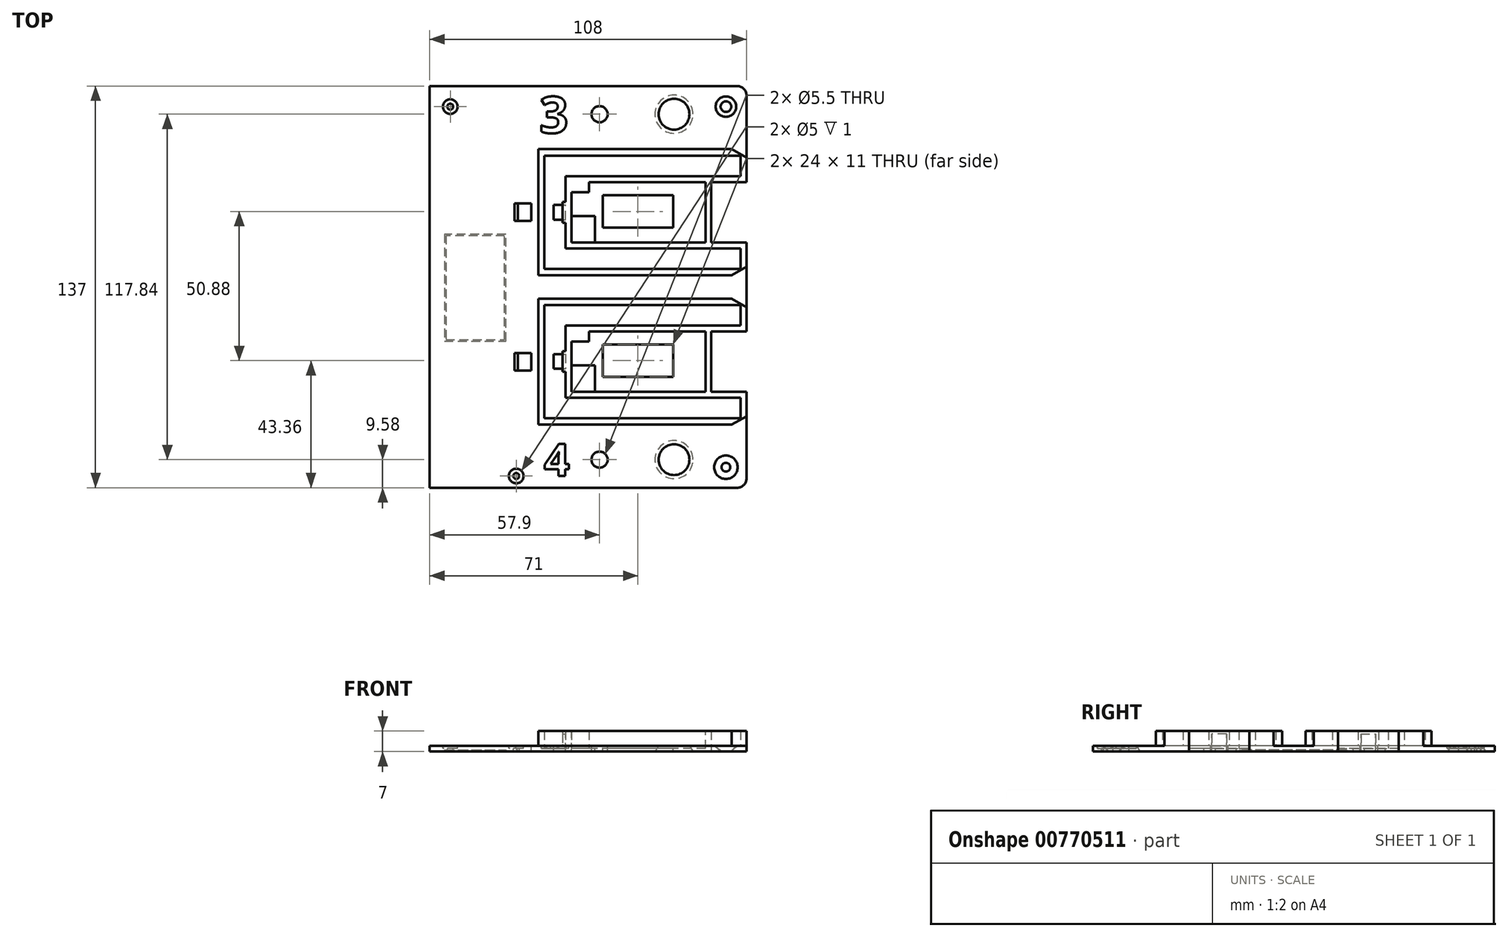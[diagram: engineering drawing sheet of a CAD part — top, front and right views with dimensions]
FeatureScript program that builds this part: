
annotation { "Feature Type Name" : "Feature", "Feature Type Description" : "" }
export const myFeature = defineFeature(function(context is Context, id is Id, definition is map)
    precondition{}
    {
        {
            var Q0;
            Q0=qCreatedBy(makeId("Top.planeOp"),FACE);
            var sketch = newSketch(context, id + "F0", { "sketchPlane" : qUnion([Q0])});
            skLineSegment(sketch, "E0.bottom", {"start": v(-108, 0) * mm, "end": v(0, 0) * mm});
            skLineSegment(sketch, "E1.right", {"start": v(-12, 4.5) * mm, "end": v(-12, 132.5) * mm, "construction": true});
            skLineSegment(sketch, "E2.top", {"start": v(-108, 21.5) * mm, "end": v(-107, 21.5) * mm});
            skLineSegment(sketch, "E2.right", {"start": v(-2, 115.5) * mm, "end": v(-2, 21.5) * mm});
            skLineSegment(sketch, "E3", {"start": v(-225.45, 68.5) * mm, "end": v(18.34, 68.5) * mm, "construction": true});
            skLineSegment(sketch, "E4", {"start": v(-12, 132.5) * mm, "end": v(-210.34, 132.5) * mm, "construction": true});
            skLineSegment(sketch, "E5", {"start": v(-12, 4.5) * mm, "end": v(-202, 4.5) * mm, "construction": true});
            skLineSegment(sketch, "E6", {"start": v(-2, 72.5) * mm, "end": v(-70.94, 72.5) * mm});
            skLineSegment(sketch, "E7", {"start": v(-70.94, 72.5) * mm, "end": v(-70.94, 115.5) * mm, "construction": true});
            skLineSegment(sketch, "E8", {"start": v(-70.94, 115.5) * mm, "end": v(-2, 115.5) * mm, "construction": true});
            skLineSegment(sketch, "E9.bottom", {"start": v(-59.7, 83.64) * mm, "end": v(-14, 83.64) * mm});
            skLineSegment(sketch, "E9.top", {"start": v(-53.7, 104.24) * mm, "end": v(-22.8, 104.24) * mm});
            skLineSegment(sketch, "E9.left", {"start": v(-59.7, 83.64) * mm, "end": v(-59.7, 100.74) * mm});
            skLineSegment(sketch, "E9.right", {"start": v(-14, 83.64) * mm, "end": v(-14, 102.84) * mm});
            skLineSegment(sketch, "E10", {"start": v(-12, 113.24) * mm, "end": v(-12, 74.64) * mm});
            skLineSegment(sketch, "E11", {"start": v(-12, 74.64) * mm, "end": v(-68.94, 74.64) * mm});
            skLineSegment(sketch, "E12", {"start": v(-68.94, 74.64) * mm, "end": v(-68.94, 113.24) * mm, "construction": true});
            skLineSegment(sketch, "E13", {"start": v(-68.94, 113.24) * mm, "end": v(-12, 113.24) * mm, "construction": true});
            skLineSegment(sketch, "E14.bottom", {"start": v(-49, 99.74) * mm, "end": v(-25, 99.74) * mm});
            skLineSegment(sketch, "E14.top", {"start": v(-49, 88.74) * mm, "end": v(-25, 88.74) * mm});
            skLineSegment(sketch, "E14.left", {"start": v(-49, 99.74) * mm, "end": v(-49, 88.74) * mm});
            skLineSegment(sketch, "E14.right", {"start": v(-25, 99.74) * mm, "end": v(-25, 88.74) * mm});
            skLineSegment(sketch, "E15", {"start": v(-25, 94.24) * mm, "end": v(-49, 94.24) * mm, "construction": true});
            skLineSegment(sketch, "E16.bottom", {"start": v(-61.7, 106.24) * mm, "end": v(-12, 106.24) * mm, "construction": true});
            skLineSegment(sketch, "E16.top", {"start": v(-61.7, 81.64) * mm, "end": v(-12, 81.64) * mm});
            skLineSegment(sketch, "E16.left", {"start": v(-61.7, 106.24) * mm, "end": v(-61.7, 81.64) * mm});
            skLineSegment(sketch, "E16.right", {"start": v(-12, 104.24) * mm, "end": v(-12, 83.64) * mm});
            skLineSegment(sketch, "E17", {"start": v(-12, 113.24) * mm, "end": v(-2, 113.24) * mm, "construction": true});
            skLineSegment(sketch, "E18", {"start": v(-12, 74.64) * mm, "end": v(-2, 74.64) * mm});
            skLineSegment(sketch, "E19", {"start": v(-12, 106.24) * mm, "end": v(-2, 106.24) * mm, "construction": true});
            skLineSegment(sketch, "E20", {"start": v(-14, 104.24) * mm, "end": v(-2, 104.24) * mm});
            skLineSegment(sketch, "E21", {"start": v(-14, 83.64) * mm, "end": v(-2, 83.64) * mm});
            skLineSegment(sketch, "E22", {"start": v(-12, 81.64) * mm, "end": v(-2, 81.64) * mm});
            skLineSegment(sketch, "E23.MirrorCS", {"start": v(-12, 23.76) * mm, "end": v(-12, 62.36) * mm});
            skLineSegment(sketch, "E24.MirrorCS", {"start": v(-59.7, 49.86) * mm, "end": v(-59.7, 32.76) * mm});
            skLineSegment(sketch, "E25.MirrorCS", {"start": v(-12, 62.36) * mm, "end": v(-2, 62.36) * mm});
            skLineSegment(sketch, "E26.MirrorCS", {"start": v(-70.94, 21.5) * mm, "end": v(-2, 21.5) * mm});
            skLineSegment(sketch, "E27.MirrorCS", {"start": v(-68.94, 62.36) * mm, "end": v(-68.94, 23.76) * mm});
            skLineSegment(sketch, "E28.MirrorCS", {"start": v(-12, 55.36) * mm, "end": v(-2, 55.36) * mm});
            skLineSegment(sketch, "E29.MirrorCS", {"start": v(-61.7, 30.76) * mm, "end": v(-61.7, 55.36) * mm});
            skLineSegment(sketch, "E30.MirrorCS", {"start": v(-59.7, 32.76) * mm, "end": v(-14, 32.76) * mm});
            skLineSegment(sketch, "E31.MirrorCS", {"start": v(-12, 23.76) * mm, "end": v(-2, 23.76) * mm});
            skLineSegment(sketch, "E32.MirrorCS", {"start": v(-12, 62.36) * mm, "end": v(-68.94, 62.36) * mm});
            skLineSegment(sketch, "E33.MirrorCS", {"start": v(-61.7, 55.36) * mm, "end": v(-12, 55.36) * mm});
            skLineSegment(sketch, "E34.MirrorCS", {"start": v(-14, 53.36) * mm, "end": v(-2, 53.36) * mm});
            skLineSegment(sketch, "E35.MirrorCS", {"start": v(-2, 64.5) * mm, "end": v(-70.94, 64.5) * mm});
            skLineSegment(sketch, "E36.MirrorCS", {"start": v(-61.7, 30.76) * mm, "end": v(-12, 30.76) * mm});
            skLineSegment(sketch, "E37.MirrorCS", {"start": v(-14, 32.76) * mm, "end": v(-2, 32.76) * mm});
            skLineSegment(sketch, "E38.MirrorCS", {"start": v(-68.94, 23.76) * mm, "end": v(-12, 23.76) * mm});
            skLineSegment(sketch, "E39.MirrorCS", {"start": v(-53.7, 53.36) * mm, "end": v(-14, 53.36) * mm});
            skLineSegment(sketch, "E40.MirrorCS", {"start": v(-12, 32.76) * mm, "end": v(-12, 53.36) * mm});
            skLineSegment(sketch, "E41.MirrorCS", {"start": v(-14, 53.36) * mm, "end": v(-14, 32.76) * mm});
            skLineSegment(sketch, "E42.MirrorCS", {"start": v(-12, 30.76) * mm, "end": v(-2, 30.76) * mm});
            skLineSegment(sketch, "E43", {"start": v(-107, 148.51) * mm, "end": v(-107, -58.81) * mm, "construction": true});
            skCircle(sketch, "E44.MirrorC", {"center": v(-50.1, 127.42) * mm, "radius": 2.75 * mm});
            skCircle(sketch, "E45.MirrorC", {"center": v(-24.7, 127.42) * mm, "radius": 5.25 * mm, "construction": true});
            skCircle(sketch, "E46.MirrorC", {"center": v(-50.1, 9.58) * mm, "radius": 2.75 * mm});
            skCircle(sketch, "E47.MirrorC", {"center": v(-24.7, 9.58) * mm, "radius": 5.25 * mm, "construction": true});
            skLineSegment(sketch, "E48.bottom", {"start": v(-49, 37.86) * mm, "end": v(-25, 37.86) * mm});
            skLineSegment(sketch, "E48.top", {"start": v(-49, 48.86) * mm, "end": v(-25, 48.86) * mm});
            skLineSegment(sketch, "E48.left", {"start": v(-49, 37.86) * mm, "end": v(-49, 48.86) * mm});
            skLineSegment(sketch, "E48.right", {"start": v(-25, 37.86) * mm, "end": v(-25, 48.86) * mm});
            skLineSegment(sketch, "E49", {"start": v(-49, 43.36) * mm, "end": v(-25, 43.36) * mm, "construction": true});
            skLineSegment(sketch, "E50", {"start": v(-2, 115.5) * mm, "end": v(0, 115.5) * mm});
            skLineSegment(sketch, "E51", {"start": v(-2, 72.5) * mm, "end": v(0, 72.5) * mm});
            skLineSegment(sketch, "E52", {"start": v(0, 137) * mm, "end": v(0, 0) * mm});
            skLineSegment(sketch, "E53", {"start": v(-59.7, 92.64) * mm, "end": v(-51.7, 92.64) * mm});
            skLineSegment(sketch, "E54", {"start": v(-51.7, 92.64) * mm, "end": v(-51.7, 83.64) * mm});
            skLineSegment(sketch, "E55", {"start": v(-59.7, 41.76) * mm, "end": v(-51.7, 41.76) * mm});
            skLineSegment(sketch, "E56", {"start": v(-51.7, 41.76) * mm, "end": v(-51.7, 32.76) * mm});
            skLineSegment(sketch, "E57", {"start": v(-53.7, 104.24) * mm, "end": v(-53.7, 100.74) * mm});
            skLineSegment(sketch, "E58", {"start": v(-53.7, 100.74) * mm, "end": v(-59.7, 100.74) * mm});
            skPoint(sketch, "E59.orphan", {"position": v(-59.7, 104.24) * mm});
            skLineSegment(sketch, "E60", {"start": v(-53.7, 53.36) * mm, "end": v(-53.7, 49.86) * mm});
            skLineSegment(sketch, "E61", {"start": v(-53.7, 49.86) * mm, "end": v(-59.7, 49.86) * mm});
            skPoint(sketch, "E62.orphan", {"position": v(-59.7, 53.36) * mm});
            skText(sketch, "E63", { "text": "3", "fontName": "OpenSans-Bold.ttf"});
            skText(sketch, "E64", { "text": "4", "fontName": "OpenSans-Bold.ttf"});
            skLineSegment(sketch, "E65", {"start": v(-182.8, 118.88) * mm, "end": v(-182.8, 145.8) * mm, "construction": true});
            skLineSegment(sketch, "E66", {"start": v(-166.65, 144.92) * mm, "end": v(-166.65, 118.26) * mm, "construction": true});
            skLineSegment(sketch, "E67", {"start": v(-108, 72.5) * mm, "end": v(-107, 72.5) * mm});
            skLineSegment(sketch, "E68", {"start": v(-108, 137) * mm, "end": v(-108, 0) * mm});
            skLineSegment(sketch, "E69.trimOffspring", {"start": v(-108, 137) * mm, "end": v(0, 137) * mm});
            skLineSegment(sketch, "E70", {"start": v(-70.94, 64.5) * mm, "end": v(-70.94, 21.5) * mm});
            skLineSegment(sketch, "E71.trimOffspring", {"start": v(-70.94, 72.5) * mm, "end": v(-64, 72.5) * mm});
            skLineSegment(sketch, "E72", {"start": v(-22.8, 104.24) * mm, "end": v(-14, 104.24) * mm});
            skLineSegment(sketch, "E73", {"start": v(-14, 104.24) * mm, "end": v(-14, 102.84) * mm});
            const initialGuessF0  = {"E63": [-0.06894, 0.004, 1, 0, 0.011], "E64": [-0.07094, 0.121, 1, 0, 0.012]};
            skSetInitialGuess(sketch, initialGuessF0);
            skSolve(sketch);
        }
        {
            var Q0;
            Q0=qCreatedBy(makeId("Top.planeOp"),FACE);
            var sketch = newSketch(context, id + "F1", { "sketchPlane" : qUnion([Q0])});
            skLineSegment(sketch, "E74.bottom", {"start": v(-108, 0) * mm, "end": v(0, 0) * mm});
            skLineSegment(sketch, "E74.top", {"start": v(-108, 137) * mm, "end": v(0, 137) * mm});
            skLineSegment(sketch, "E74.left", {"start": v(-108, 0) * mm, "end": v(-108, 137) * mm});
            skLineSegment(sketch, "E74.right", {"start": v(0, 0) * mm, "end": v(0, 137) * mm});
            skSolve(sketch);
        }
        {
            var Q0;
            Q0=qSketchRegion(id+"F1",true);
            extrude(context, id + "F2", {"entities" : qUnion([Q0]), "depth" : 2 * mm, "offsetDistance" : 25 * mm});
        }
        {
            var Q0;
            Q0=makeQuery(id+"F2.opExtrude","CAP_FACE",FACE,{"disambiguationData":[OSD([sQuery(id+"F1.wireOp",EDGE,"E74.bottom"),sQuery(id+"F1.wireOp",EDGE,"E74.top"),sQuery(id+"F1.wireOp",EDGE,"E74.left"),sQuery(id+"F1.wireOp",EDGE,"E74.right")])],"isStart":false});
            var sketch = newSketch(context, id + "F3", { "sketchPlane" : qUnion([Q0])});
            skLineSegment(sketch, "E75.bottom", {"start": v(-70.94, 115.5) * mm, "end": v(0, 115.5) * mm});
            skLineSegment(sketch, "E75.top", {"start": v(-70.94, 72.5) * mm, "end": v(0, 72.5) * mm});
            skLineSegment(sketch, "E75.left", {"start": v(-70.94, 115.5) * mm, "end": v(-70.94, 72.5) * mm});
            skLineSegment(sketch, "E75.right", {"start": v(0, 115.5) * mm, "end": v(0, 72.5) * mm});
            skLineSegment(sketch, "E76.bottom", {"start": v(-68.94, 62.36) * mm, "end": v(-2, 62.36) * mm});
            skLineSegment(sketch, "E76.top", {"start": v(-68.94, 23.76) * mm, "end": v(-2, 23.76) * mm});
            skLineSegment(sketch, "E76.left", {"start": v(-68.94, 62.36) * mm, "end": v(-68.94, 23.76) * mm});
            skLineSegment(sketch, "E76.right", {"start": v(0, 62.36) * mm, "end": v(0, 23.76) * mm});
            skLineSegment(sketch, "E77.bottom", {"start": v(-70.94, 64.5) * mm, "end": v(0, 64.5) * mm});
            skLineSegment(sketch, "E77.top", {"start": v(-70.94, 21.5) * mm, "end": v(0, 21.5) * mm});
            skLineSegment(sketch, "E77.left", {"start": v(-70.94, 64.5) * mm, "end": v(-70.94, 21.5) * mm});
            skLineSegment(sketch, "E77.right", {"start": v(0, 64.5) * mm, "end": v(0, 21.5) * mm});
            skLineSegment(sketch, "E78.bottom", {"start": v(-68.94, 113.24) * mm, "end": v(-2, 113.24) * mm});
            skLineSegment(sketch, "E78.top", {"start": v(-68.94, 74.64) * mm, "end": v(-2, 74.64) * mm});
            skLineSegment(sketch, "E78.left", {"start": v(-68.94, 113.24) * mm, "end": v(-68.94, 74.64) * mm});
            skLineSegment(sketch, "E78.right", {"start": v(-2, 113.24) * mm, "end": v(-2, 74.64) * mm});
            skLineSegment(sketch, "E79", {"start": v(-2, 62.36) * mm, "end": v(-2, 23.76) * mm});
            skLineSegment(sketch, "E80.bottom", {"start": v(-12, 104.24) * mm, "end": v(-2, 104.24) * mm});
            skLineSegment(sketch, "E80.top", {"start": v(-12, 83.64) * mm, "end": v(-2, 83.64) * mm});
            skLineSegment(sketch, "E80.left", {"start": v(-12, 104.24) * mm, "end": v(-12, 83.64) * mm});
            skLineSegment(sketch, "E80.right", {"start": v(-2, 104.24) * mm, "end": v(-2, 83.64) * mm});
            skLineSegment(sketch, "E81.bottom", {"start": v(-12, 53.36) * mm, "end": v(-2, 53.36) * mm});
            skLineSegment(sketch, "E81.top", {"start": v(-12, 32.76) * mm, "end": v(-2, 32.76) * mm});
            skLineSegment(sketch, "E81.left", {"start": v(-12, 53.36) * mm, "end": v(-12, 32.76) * mm});
            skLineSegment(sketch, "E81.right", {"start": v(-2, 53.36) * mm, "end": v(-2, 32.76) * mm});
            skLineSegment(sketch, "E82.bottom", {"start": v(-61.7, 55.36) * mm, "end": v(-2, 55.36) * mm});
            skLineSegment(sketch, "E82.top", {"start": v(-61.7, 30.76) * mm, "end": v(-2, 30.76) * mm});
            skLineSegment(sketch, "E82.left", {"start": v(-61.7, 55.36) * mm, "end": v(-61.7, 30.76) * mm});
            skLineSegment(sketch, "E83.bottom", {"start": v(-61.7, 106.24) * mm, "end": v(-2, 106.24) * mm});
            skLineSegment(sketch, "E83.top", {"start": v(-61.7, 81.64) * mm, "end": v(-2, 81.64) * mm});
            skLineSegment(sketch, "E83.left", {"start": v(-61.7, 106.24) * mm, "end": v(-61.7, 81.64) * mm});
            skLineSegment(sketch, "E84", {"start": v(-14, 102.84) * mm, "end": v(-14, 83.64) * mm});
            skLineSegment(sketch, "E85", {"start": v(-14, 102.84) * mm, "end": v(-22.8, 102.84) * mm});
            skLineSegment(sketch, "E86", {"start": v(-22.8, 102.84) * mm, "end": v(-22.8, 104.24) * mm});
            skLineSegment(sketch, "E87", {"start": v(-22.8, 104.24) * mm, "end": v(-53.7, 104.24) * mm});
            skLineSegment(sketch, "E88", {"start": v(-53.7, 104.24) * mm, "end": v(-53.7, 100.74) * mm});
            skLineSegment(sketch, "E89", {"start": v(-53.7, 100.74) * mm, "end": v(-59.7, 100.74) * mm});
            skLineSegment(sketch, "E90", {"start": v(-59.7, 100.74) * mm, "end": v(-59.7, 92.64) * mm});
            skLineSegment(sketch, "E91", {"start": v(-59.7, 92.64) * mm, "end": v(-51.7, 92.64) * mm});
            skLineSegment(sketch, "E92", {"start": v(-51.7, 92.64) * mm, "end": v(-51.7, 83.64) * mm});
            skLineSegment(sketch, "E93", {"start": v(-51.7, 83.64) * mm, "end": v(-14, 83.64) * mm});
            skLineSegment(sketch, "E94", {"start": v(-14, 51.96) * mm, "end": v(-22.8, 51.96) * mm});
            skLineSegment(sketch, "E95", {"start": v(-22.8, 51.96) * mm, "end": v(-22.8, 53.36) * mm});
            skLineSegment(sketch, "E96", {"start": v(-22.8, 53.36) * mm, "end": v(-53.7, 53.36) * mm});
            skLineSegment(sketch, "E97", {"start": v(-53.7, 53.36) * mm, "end": v(-53.7, 49.86) * mm});
            skLineSegment(sketch, "E98", {"start": v(-53.7, 49.86) * mm, "end": v(-59.7, 49.86) * mm});
            skLineSegment(sketch, "E99", {"start": v(-59.7, 49.86) * mm, "end": v(-59.7, 41.76) * mm});
            skLineSegment(sketch, "E100", {"start": v(-59.7, 41.76) * mm, "end": v(-51.7, 41.76) * mm});
            skLineSegment(sketch, "E101", {"start": v(-51.7, 41.76) * mm, "end": v(-51.7, 32.76) * mm});
            skLineSegment(sketch, "E102", {"start": v(-51.7, 32.76) * mm, "end": v(-14, 32.76) * mm});
            skLineSegment(sketch, "E103", {"start": v(-14, 32.76) * mm, "end": v(-14, 51.96) * mm});
            skSolve(sketch);
        }
        {
            var Q0;
            Q0=qSketchRegion(id+"F3",true);
            var Q1;
            {var subQ1=sQuery(id+"F3.wireOp",EDGE,"E80.bottom");Q1=makeQuery(id+"F3.imprint","IMPRINT",FACE,{"disambiguationData":[TD([[makeQuery(id+"F3.imprint","IMPRINT",EDGE,{"derivedFrom":subQ1}),1.0]])]});}
            var Q2;
            {var subQ2=sQuery(id+"F3.wireOp",EDGE,"E81.bottom");Q2=makeQuery(id+"F3.imprint","IMPRINT",FACE,{"disambiguationData":[TD([[makeQuery(id+"F3.imprint","IMPRINT",EDGE,{"derivedFrom":subQ2}),1.0]])]});}
            extrude(context, id + "F4", {"entities" : qUnion([Q0, Q1, Q2]), "operationType" : NewBodyOperationType.ADD, "depth" : 5 * mm, "offsetDistance" : 25 * mm});
        }
        {
            var Q0;
            {var subQ0=sQuery(id+"F1.wireOp",EDGE,"E74.bottom");var subQ1=sQuery(id+"F1.wireOp",EDGE,"E74.right");var subQ2=sQuery(id+"F1.wireOp",EDGE,"E74.top");var subQ3=sQuery(id+"F1.wireOp",EDGE,"E74.left");Q0=makeQuery(id+"F4.boolean.opBoolean","SPLIT",FACE,{"disambiguationData":[TD([makeQuery(id+"F2.opExtrude","SWEPT_FACE",FACE,{"disambiguationData":[OSD([subQ0])]})])],"derivedFrom":makeQuery(id+"F2.opExtrude","CAP_FACE",FACE,{"disambiguationData":[OSD([subQ0,subQ2,subQ3,subQ1])],"isStart":false})});}
            var sketch = newSketch(context, id + "F5", { "sketchPlane" : qUnion([Q0])});
            skCircle(sketch, "E104", {"center": v(-24.7, 127.42) * mm, "radius": 5.25 * mm});
            skCircle(sketch, "E105", {"center": v(-50.1, 127.42) * mm, "radius": 2.75 * mm});
            skCircle(sketch, "E106", {"center": v(-24.7, 9.58) * mm, "radius": 5.25 * mm});
            skCircle(sketch, "E107", {"center": v(-50.1, 9.58) * mm, "radius": 2.75 * mm});
            skLineSegment(sketch, "E108.bottom", {"start": v(-12, 83.64) * mm, "end": v(-2, 83.64) * mm});
            skLineSegment(sketch, "E108.top", {"start": v(-12, 104.24) * mm, "end": v(-2, 104.24) * mm});
            skLineSegment(sketch, "E108.left", {"start": v(-12, 83.64) * mm, "end": v(-12, 104.24) * mm});
            skLineSegment(sketch, "E108.right", {"start": v(-2, 83.64) * mm, "end": v(-2, 104.24) * mm});
            skLineSegment(sketch, "E109.bottom", {"start": v(-12, 32.76) * mm, "end": v(-2, 32.76) * mm});
            skLineSegment(sketch, "E109.top", {"start": v(-12, 53.36) * mm, "end": v(-2, 53.36) * mm});
            skLineSegment(sketch, "E109.left", {"start": v(-12, 32.76) * mm, "end": v(-12, 53.36) * mm});
            skLineSegment(sketch, "E109.right", {"start": v(-2, 32.76) * mm, "end": v(-2, 53.36) * mm});
            skLineSegment(sketch, "E110.bottom", {"start": v(-49, 88.74) * mm, "end": v(-25, 88.74) * mm});
            skLineSegment(sketch, "E110.top", {"start": v(-49, 99.74) * mm, "end": v(-25, 99.74) * mm});
            skLineSegment(sketch, "E110.left", {"start": v(-49, 88.74) * mm, "end": v(-49, 99.74) * mm});
            skLineSegment(sketch, "E110.right", {"start": v(-25, 88.74) * mm, "end": v(-25, 99.74) * mm});
            skLineSegment(sketch, "E111.bottom", {"start": v(-49, 37.86) * mm, "end": v(-25, 37.86) * mm});
            skLineSegment(sketch, "E111.top", {"start": v(-49, 48.86) * mm, "end": v(-25, 48.86) * mm});
            skLineSegment(sketch, "E111.left", {"start": v(-49, 37.86) * mm, "end": v(-49, 48.86) * mm});
            skLineSegment(sketch, "E111.right", {"start": v(-25, 37.86) * mm, "end": v(-25, 48.86) * mm});
            skSolve(sketch);
        }
        {
            var Q0;
            Q0=qSketchRegion(id+"F5",true);
            extrude(context, id + "F6", {"entities" : qUnion([Q0]), "operationType" : NewBodyOperationType.REMOVE, "oppositeDirection" : true, "depth" : 2 * mm, "offsetDistance" : 25 * mm});
        }
        {
            var Q0;
            {var subQ0=sQuery(id+"F1.wireOp",EDGE,"E74.bottom");var subQ1=sQuery(id+"F1.wireOp",EDGE,"E74.right");var subQ2=sQuery(id+"F1.wireOp",EDGE,"E74.top");var subQ3=sQuery(id+"F1.wireOp",EDGE,"E74.left");Q0=makeQuery(id+"F4.boolean.opBoolean","SPLIT",FACE,{"disambiguationData":[TD([makeQuery(id+"F2.opExtrude","SWEPT_FACE",FACE,{"disambiguationData":[OSD([subQ0])]})])],"derivedFrom":makeQuery(id+"F2.opExtrude","CAP_FACE",FACE,{"disambiguationData":[OSD([subQ0,subQ2,subQ3,subQ1])],"isStart":false})});}
            var sketch = newSketch(context, id + "F7", { "sketchPlane" : qUnion([Q0])});
            skCircle(sketch, "E112", {"center": v(-7, 130) * mm, "radius": 4 * mm, "construction": true});
            skCircle(sketch, "E113", {"center": v(-101, 130) * mm, "radius": 1 * mm});
            skCircle(sketch, "E114", {"center": v(-7, 7) * mm, "radius": 4 * mm, "construction": true});
            skCircle(sketch, "E115", {"center": v(-78.5, 4) * mm, "radius": 1 * mm});
            skSolve(sketch);
        }
        {
            var Q0;
            Q0=qSketchRegion(id+"F7",true);
            var Q1;
            Q1=qConstructionFilter(qBodyType(qCreatedBy(id+"F7",EDGE),BodyType.WIRE),ConstructionObject.NO);
            extrude(context, id + "F8", {"entities" : qUnion([Q0]), "operationType" : NewBodyOperationType.REMOVE, "surfaceEntities" : qUnion([Q1]), "oppositeDirection" : true, "depth" : 2 * mm, "offsetDistance" : 25 * mm});
        }
        {
            var Q0;
            Q0=makeQuery(id+"F2.opExtrude","SWEPT_EDGE",EDGE,{"disambiguationData":[OSD([sQuery(id+"F1.wireOp",EDGE,"E74.top"),sQuery(id+"F1.wireOp",EDGE,"E74.right")])]});
            var Q1;
            Q1=makeQuery(id+"F2.opExtrude","SWEPT_EDGE",EDGE,{"disambiguationData":[OSD([sQuery(id+"F1.wireOp",EDGE,"E74.bottom"),sQuery(id+"F1.wireOp",EDGE,"E74.right")])]});
            fillet(context, id + "F9", {"entities" : qUnion([Q0, Q1]), "radius" : 3.17 * mm, "tangentPropagation" : true, "allowEdgeOverflow" : false});
        }
        {
            var Q0;
            {var subQ0=sQuery(id+"F1.wireOp",EDGE,"E74.bottom");var subQ1=sQuery(id+"F1.wireOp",EDGE,"E74.right");var subQ2=sQuery(id+"F1.wireOp",EDGE,"E74.top");var subQ3=sQuery(id+"F1.wireOp",EDGE,"E74.left");Q0=makeQuery(id+"F4.boolean.opBoolean","SPLIT",FACE,{"disambiguationData":[TD([makeQuery(id+"F2.opExtrude","SWEPT_FACE",FACE,{"disambiguationData":[OSD([subQ0])]})])],"derivedFrom":makeQuery(id+"F2.opExtrude","CAP_FACE",FACE,{"disambiguationData":[OSD([subQ0,subQ2,subQ3,subQ1])],"isStart":false})});}
            var sketch = newSketch(context, id + "F10", { "sketchPlane" : qUnion([Q0])});
            skText(sketch, "E116", { "text": "3", "fontName": "OpenSans-Bold.ttf"});
            skText(sketch, "E117", { "text": "4", "fontName": "OpenSans-Bold.ttf"});
            const initialGuessF10  = {"E116": [-0.07066, 0.121, 1, 0, 0.01246], "E117": [-0.069, 0.004, 1, 0, 0.011]};
            skSetInitialGuess(sketch, initialGuessF10);
            skSolve(sketch);
        }
        {
            var Q0;
            Q0=qSketchRegion(id+"F10",true);
            extrude(context, id + "F11", {"entities" : qUnion([Q0]), "operationType" : NewBodyOperationType.REMOVE, "oppositeDirection" : true, "depth" : 1 * mm, "offsetDistance" : 25 * mm});
        }
        {
            var Q0;
            Q0=makeQuery(id+"F4.opExtrude","CAP_FACE",FACE,{"disambiguationData":[OSD([sQuery(id+"F3.wireOp",EDGE,"E75.bottom"),sQuery(id+"F3.wireOp",EDGE,"E75.top"),sQuery(id+"F3.wireOp",EDGE,"E75.left"),sQuery(id+"F3.wireOp",EDGE,"E75.right"),sQuery(id+"F3.wireOp",EDGE,"E78.bottom"),sQuery(id+"F3.wireOp",EDGE,"E78.top"),sQuery(id+"F3.wireOp",EDGE,"E78.left"),sQuery(id+"F3.wireOp",EDGE,"E78.right"),sQuery(id+"F3.wireOp",EDGE,"E80.bottom"),sQuery(id+"F3.wireOp",EDGE,"E80.top"),sQuery(id+"F3.wireOp",EDGE,"E80.left"),sQuery(id+"F3.wireOp",EDGE,"E80.right"),sQuery(id+"F3.wireOp",EDGE,"E83.bottom"),sQuery(id+"F3.wireOp",EDGE,"E83.top"),sQuery(id+"F3.wireOp",EDGE,"E83.left"),sQuery(id+"F3.wireOp",EDGE,"E84"),sQuery(id+"F3.wireOp",EDGE,"E85"),sQuery(id+"F3.wireOp",EDGE,"E86"),sQuery(id+"F3.wireOp",EDGE,"E87"),sQuery(id+"F3.wireOp",EDGE,"E88"),sQuery(id+"F3.wireOp",EDGE,"E89"),sQuery(id+"F3.wireOp",EDGE,"E90"),sQuery(id+"F3.wireOp",EDGE,"E91"),sQuery(id+"F3.wireOp",EDGE,"E92"),sQuery(id+"F3.wireOp",EDGE,"E93")])],"isStart":false});
            var sketch = newSketch(context, id + "F12", { "sketchPlane" : qUnion([Q0])});
            skLineSegment(sketch, "E118.bottom", {"start": v(-59.7, 83.64) * mm, "end": v(-51.7, 83.64) * mm});
            skLineSegment(sketch, "E118.top", {"start": v(-59.7, 92.64) * mm, "end": v(-51.7, 92.64) * mm});
            skLineSegment(sketch, "E118.left", {"start": v(-59.7, 83.64) * mm, "end": v(-59.7, 92.64) * mm});
            skLineSegment(sketch, "E118.right", {"start": v(-51.7, 83.64) * mm, "end": v(-51.7, 92.64) * mm});
            skLineSegment(sketch, "E119.bottom", {"start": v(-59.7, 32.76) * mm, "end": v(-51.7, 32.76) * mm});
            skLineSegment(sketch, "E119.top", {"start": v(-59.7, 41.76) * mm, "end": v(-51.7, 41.76) * mm});
            skLineSegment(sketch, "E119.left", {"start": v(-59.7, 32.76) * mm, "end": v(-59.7, 41.76) * mm});
            skLineSegment(sketch, "E119.right", {"start": v(-51.7, 32.76) * mm, "end": v(-51.7, 41.76) * mm});
            skLineSegment(sketch, "E120.bottom", {"start": v(-4.45, 83.64) * mm, "end": v(2.07, 83.64) * mm});
            skLineSegment(sketch, "E120.top", {"start": v(-4.45, 104.24) * mm, "end": v(2.07, 104.24) * mm});
            skLineSegment(sketch, "E120.left", {"start": v(-4.45, 83.64) * mm, "end": v(-4.45, 104.24) * mm});
            skLineSegment(sketch, "E120.right", {"start": v(2.07, 83.64) * mm, "end": v(2.07, 104.24) * mm});
            skLineSegment(sketch, "E121.bottom", {"start": v(-6.26, 53.36) * mm, "end": v(9.3, 53.36) * mm});
            skLineSegment(sketch, "E121.top", {"start": v(-6.26, 32.76) * mm, "end": v(9.3, 32.76) * mm});
            skLineSegment(sketch, "E121.left", {"start": v(-6.26, 53.36) * mm, "end": v(-6.26, 32.76) * mm});
            skLineSegment(sketch, "E121.right", {"start": v(9.3, 53.36) * mm, "end": v(9.3, 32.76) * mm});
            skSolve(sketch);
        }
        {
            var Q0;
            Q0=qSketchRegion(id+"F12",true);
            extrude(context, id + "F13", {"entities" : qUnion([Q0]), "operationType" : NewBodyOperationType.REMOVE, "endBound" : BoundingType.THROUGH_ALL, "oppositeDirection" : true, "depth" : 25 * mm, "offsetDistance" : 25 * mm});
        }
        {
            var Q0;
            Q0=makeQuery(id+"F2.opExtrude","CAP_FACE",FACE,{"disambiguationData":[OSD([sQuery(id+"F1.wireOp",EDGE,"E74.bottom"),sQuery(id+"F1.wireOp",EDGE,"E74.top"),sQuery(id+"F1.wireOp",EDGE,"E74.left"),sQuery(id+"F1.wireOp",EDGE,"E74.right")])],"isStart":true});
            var sketch = newSketch(context, id + "F14", { "sketchPlane" : qUnion([Q0])});
            skCircle(sketch, "E122", {"center": v(-7, -130) * mm, "radius": 1.81 * mm});
            skSolve(sketch);
        }
        {
            var Q0;
            {var subQ6=sQuery(id+"F1.wireOp",EDGE,"E74.right");var subQ8=sQuery(id+"F1.wireOp",EDGE,"E74.top");var subQ11=sQuery(id+"F1.wireOp",EDGE,"E74.left");var subQ14=sQuery(id+"F1.wireOp",EDGE,"E74.bottom");var subQ15=makeQuery(id+"F2.opExtrude","SWEPT_FACE",FACE,{"disambiguationData":[OSD([subQ14])]});Q0=makeQuery(id+"F11.boolean.opBoolean","SPLIT",FACE,{"disambiguationData":[TD([subQ15])],"derivedFrom":makeQuery(id+"F4.boolean.opBoolean","SPLIT",FACE,{"disambiguationData":[TD([subQ15])],"derivedFrom":makeQuery(id+"F2.opExtrude","CAP_FACE",FACE,{"disambiguationData":[OSD([subQ14,subQ8,subQ11,subQ6])],"isStart":false})})});}
            var sketch = newSketch(context, id + "F15", { "sketchPlane" : qUnion([Q0])});
            skCircle(sketch, "E123", {"center": v(-7, 130) * mm, "radius": 3.5 * mm});
            skSolve(sketch);
        }
        {
            var Q1;
            Q1=qSketchRegion(id+"F15",true);
            var Q2;
            Q2=qSketchRegion(id+"F14",true);
            loft(context, id + "F16", {"operationType" : NewBodyOperationType.REMOVE, "sheetProfilesArray" : [{ "sheetProfileEntities" : qUnion([Q1]) }, { "sheetProfileEntities" : qUnion([Q2]) }]});
        }
        {
            var Q0;
            {var subQ6=sQuery(id+"F1.wireOp",EDGE,"E74.right");var subQ8=sQuery(id+"F1.wireOp",EDGE,"E74.top");var subQ11=sQuery(id+"F1.wireOp",EDGE,"E74.left");var subQ14=sQuery(id+"F1.wireOp",EDGE,"E74.bottom");var subQ15=makeQuery(id+"F2.opExtrude","SWEPT_FACE",FACE,{"disambiguationData":[OSD([subQ14])]});Q0=makeQuery(id+"F11.boolean.opBoolean","SPLIT",FACE,{"disambiguationData":[TD([subQ15])],"derivedFrom":makeQuery(id+"F4.boolean.opBoolean","SPLIT",FACE,{"disambiguationData":[TD([subQ15])],"derivedFrom":makeQuery(id+"F2.opExtrude","CAP_FACE",FACE,{"disambiguationData":[OSD([subQ14,subQ8,subQ11,subQ6])],"isStart":false})})});}
            var sketch = newSketch(context, id + "F17", { "sketchPlane" : qUnion([Q0])});
            skCircle(sketch, "E124", {"center": v(-7, 7) * mm, "radius": 4 * mm});
            skSolve(sketch);
        }
        {
            var Q0;
            Q0=makeQuery(id+"F2.opExtrude","CAP_FACE",FACE,{"disambiguationData":[OSD([sQuery(id+"F1.wireOp",EDGE,"E74.bottom"),sQuery(id+"F1.wireOp",EDGE,"E74.top"),sQuery(id+"F1.wireOp",EDGE,"E74.left"),sQuery(id+"F1.wireOp",EDGE,"E74.right")])],"isStart":true});
            var sketch = newSketch(context, id + "F18", { "sketchPlane" : qUnion([Q0])});
            skCircle(sketch, "E125", {"center": v(-7, -7) * mm, "radius": 1.5 * mm});
            skSolve(sketch);
        }
        {
            var Q1;
            Q1=qSketchRegion(id+"F18",true);
            var Q2;
            Q2=qSketchRegion(id+"F17",true);
            loft(context, id + "F19", {"operationType" : NewBodyOperationType.REMOVE, "sheetProfilesArray" : [{ "sheetProfileEntities" : qUnion([Q1]) }, { "sheetProfileEntities" : qUnion([Q2]) }]});
        }
        {
            var Q0;
            {var subQ6=sQuery(id+"F1.wireOp",EDGE,"E74.right");var subQ8=sQuery(id+"F1.wireOp",EDGE,"E74.top");var subQ11=sQuery(id+"F1.wireOp",EDGE,"E74.left");var subQ14=sQuery(id+"F1.wireOp",EDGE,"E74.bottom");var subQ15=makeQuery(id+"F2.opExtrude","SWEPT_FACE",FACE,{"disambiguationData":[OSD([subQ14])]});Q0=makeQuery(id+"F11.boolean.opBoolean","SPLIT",FACE,{"disambiguationData":[TD([subQ15])],"derivedFrom":makeQuery(id+"F4.boolean.opBoolean","SPLIT",FACE,{"disambiguationData":[TD([subQ15])],"derivedFrom":makeQuery(id+"F2.opExtrude","CAP_FACE",FACE,{"disambiguationData":[OSD([subQ14,subQ8,subQ11,subQ6])],"isStart":false})})});}
            var sketch = newSketch(context, id + "F20", { "sketchPlane" : qUnion([Q0])});
            skCircle(sketch, "E126", {"center": v(-101, 130) * mm, "radius": 2.5 * mm});
            skCircle(sketch, "E127", {"center": v(-78.5, 4) * mm, "radius": 2.5 * mm});
            skSolve(sketch);
        }
        {
            var Q0;
            Q0=qSketchRegion(id+"F20",true);
            extrude(context, id + "F21", {"entities" : qUnion([Q0]), "operationType" : NewBodyOperationType.REMOVE, "oppositeDirection" : true, "depth" : 1 * mm, "offsetDistance" : 25 * mm});
        }
        {
            var Q0;
            Q0=makeQuery(id+"F4.boolean.opBoolean","SPLIT",FACE,{"disambiguationData":[TD([makeQuery(id+"F4.opExtrude","SWEPT_FACE",FACE,{"disambiguationData":[OSD([sQuery(id+"F3.wireOp",EDGE,"E84")])]})])],"derivedFrom":makeQuery(id+"F2.opExtrude","CAP_FACE",FACE,{"disambiguationData":[OSD([sQuery(id+"F1.wireOp",EDGE,"E74.bottom"),sQuery(id+"F1.wireOp",EDGE,"E74.top"),sQuery(id+"F1.wireOp",EDGE,"E74.left"),sQuery(id+"F1.wireOp",EDGE,"E74.right")])],"isStart":false})});
            var sketch = newSketch(context, id + "F22", { "sketchPlane" : qUnion([Q0])});
            skLineSegment(sketch, "E128", {"start": v(-53.7, 100.74) * mm, "end": v(-53.7, 104.24) * mm});
            skLineSegment(sketch, "E129", {"start": v(-53.7, 104.24) * mm, "end": v(-22.8, 104.24) * mm});
            skLineSegment(sketch, "E130", {"start": v(-22.8, 104.24) * mm, "end": v(-22.8, 102.84) * mm});
            skLineSegment(sketch, "E131", {"start": v(-22.8, 102.84) * mm, "end": v(-14, 102.84) * mm});
            skLineSegment(sketch, "E132", {"start": v(-14, 102.84) * mm, "end": v(-14, 83.64) * mm});
            skLineSegment(sketch, "E133", {"start": v(-14, 83.64) * mm, "end": v(-59.7, 83.64) * mm});
            skLineSegment(sketch, "E134", {"start": v(-59.7, 83.64) * mm, "end": v(-59.7, 100.74) * mm});
            skLineSegment(sketch, "E135", {"start": v(-59.7, 100.74) * mm, "end": v(-53.7, 100.74) * mm});
            skLineSegment(sketch, "E136", {"start": v(-53.7, 53.36) * mm, "end": v(-22.8, 53.36) * mm});
            skLineSegment(sketch, "E137", {"start": v(-22.8, 53.36) * mm, "end": v(-22.8, 51.96) * mm});
            skLineSegment(sketch, "E138", {"start": v(-22.8, 51.96) * mm, "end": v(-14, 51.96) * mm});
            skLineSegment(sketch, "E139", {"start": v(-14, 51.96) * mm, "end": v(-14, 32.76) * mm});
            skLineSegment(sketch, "E140", {"start": v(-14, 32.76) * mm, "end": v(-59.7, 32.76) * mm});
            skLineSegment(sketch, "E141", {"start": v(-59.7, 32.76) * mm, "end": v(-59.7, 49.86) * mm});
            skLineSegment(sketch, "E142", {"start": v(-59.7, 49.86) * mm, "end": v(-53.7, 49.86) * mm});
            skLineSegment(sketch, "E143", {"start": v(-53.7, 49.86) * mm, "end": v(-53.7, 53.36) * mm});
            skSolve(sketch);
        }
        {
            var Q0;
            Q0=qSketchRegion(id+"F22",true);
            extrude(context, id + "F23", {"entities" : qUnion([Q0]), "operationType" : NewBodyOperationType.REMOVE, "oppositeDirection" : true, "depth" : 1 * mm, "offsetDistance" : 25 * mm});
        }
        {
            var Q0;
            Q0=makeQuery(id+"F2.opExtrude","CAP_FACE",FACE,{"disambiguationData":[OSD([sQuery(id+"F1.wireOp",EDGE,"E74.bottom"),sQuery(id+"F1.wireOp",EDGE,"E74.top"),sQuery(id+"F1.wireOp",EDGE,"E74.left"),sQuery(id+"F1.wireOp",EDGE,"E74.right")])],"isStart":true});
            var sketch = newSketch(context, id + "F24", { "sketchPlane" : qUnion([Q0])});
            skLineSegment(sketch, "E144", {"start": v(-102.5, -50.5) * mm, "end": v(-82.5, -50.5) * mm});
            skLineSegment(sketch, "E145", {"start": v(-82.5, -50.5) * mm, "end": v(-82.5, -75.5) * mm});
            skLineSegment(sketch, "E146", {"start": v(-82.5, -75.5) * mm, "end": v(-82.5, -86) * mm});
            skLineSegment(sketch, "E147", {"start": v(-82.5, -86) * mm, "end": v(-102.5, -86) * mm});
            skLineSegment(sketch, "E148", {"start": v(-102.5, -86) * mm, "end": v(-102.5, -50.5) * mm});
            skLineSegment(sketch, "E149", {"start": v(-103, -50) * mm, "end": v(-82, -50) * mm});
            skLineSegment(sketch, "E150", {"start": v(-82, -50) * mm, "end": v(-82, -68.5) * mm});
            skLineSegment(sketch, "E151", {"start": v(-82, -68.5) * mm, "end": v(-82, -86.5) * mm});
            skLineSegment(sketch, "E152", {"start": v(-82, -86.5) * mm, "end": v(-103, -86.5) * mm});
            skLineSegment(sketch, "E153", {"start": v(-103, -86.5) * mm, "end": v(-103, -50) * mm});
            skPoint(sketch, "E154.startSnap0", {"position": v(-108, -68.5) * mm});
            skLineSegment(sketch, "E155", {"start": v(-118.15, -68.5) * mm, "end": v(43.88, -68.5) * mm, "construction": true});
            skSolve(sketch);
        }
        {
            var Q0;
            Q0=qSketchRegion(id+"F24",true);
            extrude(context, id + "F25", {"entities" : qUnion([Q0]), "operationType" : NewBodyOperationType.REMOVE, "oppositeDirection" : true, "depth" : 0.5 * mm, "offsetDistance" : 25 * mm});
        }
        {
            var Q0;
            {var subQ1=sQuery(id+"F3.wireOp",EDGE,"E78.bottom");Q0=makeQuery(id+"F4.boolean.opBoolean","SPLIT",FACE,{"disambiguationData":[TD([makeQuery(id+"F4.opExtrude","SWEPT_FACE",FACE,{"disambiguationData":[OSD([subQ1])]})])],"derivedFrom":makeQuery(id+"F2.opExtrude","CAP_FACE",FACE,{"disambiguationData":[OSD([sQuery(id+"F1.wireOp",EDGE,"E74.bottom"),sQuery(id+"F1.wireOp",EDGE,"E74.top"),sQuery(id+"F1.wireOp",EDGE,"E74.left"),sQuery(id+"F1.wireOp",EDGE,"E74.right")])],"isStart":false})});}
            var sketch = newSketch(context, id + "F26", { "sketchPlane" : qUnion([Q0])});
            skLineSegment(sketch, "E156.bottom", {"start": v(-65.7, 40.56) * mm, "end": v(-61.7, 40.56) * mm});
            skLineSegment(sketch, "E156.top", {"start": v(-65.7, 45.56) * mm, "end": v(-61.7, 45.56) * mm});
            skLineSegment(sketch, "E156.left", {"start": v(-65.7, 40.56) * mm, "end": v(-65.7, 45.56) * mm});
            skLineSegment(sketch, "E156.right", {"start": v(-61.7, 40.56) * mm, "end": v(-61.7, 45.56) * mm});
            skLineSegment(sketch, "E157", {"start": v(-89.61, 43.06) * mm, "end": v(15.59, 43.06) * mm, "construction": true});
            skLineSegment(sketch, "E158", {"start": v(-87.44, 93.94) * mm, "end": v(20.14, 93.94) * mm, "construction": true});
            skPoint(sketch, "E158.startSnap0", {"position": v(-68.94, 93.94) * mm});
            skLineSegment(sketch, "E159.bottom", {"start": v(-65.7, 96.44) * mm, "end": v(-61.7, 96.44) * mm});
            skLineSegment(sketch, "E159.top", {"start": v(-65.7, 91.44) * mm, "end": v(-61.7, 91.44) * mm});
            skLineSegment(sketch, "E159.left", {"start": v(-65.7, 96.44) * mm, "end": v(-65.7, 91.44) * mm});
            skLineSegment(sketch, "E159.right", {"start": v(-61.7, 96.44) * mm, "end": v(-61.7, 91.44) * mm});
            skSolve(sketch);
        }
        {
            var Q0;
            Q0=qSketchRegion(id+"F26",true);
            extrude(context, id + "F27", {"entities" : qUnion([Q0]), "operationType" : NewBodyOperationType.REMOVE, "endBound" : BoundingType.THROUGH_ALL, "oppositeDirection" : true, "depth" : 25 * mm, "offsetDistance" : 25 * mm});
        }
        {
            var Q0;
            {var subQ6=sQuery(id+"F1.wireOp",EDGE,"E74.right");var subQ8=sQuery(id+"F1.wireOp",EDGE,"E74.top");var subQ11=sQuery(id+"F1.wireOp",EDGE,"E74.left");var subQ14=sQuery(id+"F1.wireOp",EDGE,"E74.bottom");var subQ15=makeQuery(id+"F2.opExtrude","SWEPT_FACE",FACE,{"disambiguationData":[OSD([subQ14])]});Q0=makeQuery(id+"F11.boolean.opBoolean","SPLIT",FACE,{"disambiguationData":[TD([subQ15])],"derivedFrom":makeQuery(id+"F4.boolean.opBoolean","SPLIT",FACE,{"disambiguationData":[TD([subQ15])],"derivedFrom":makeQuery(id+"F2.opExtrude","CAP_FACE",FACE,{"disambiguationData":[OSD([subQ14,subQ8,subQ11,subQ6])],"isStart":false})})});}
            var sketch = newSketch(context, id + "F28", { "sketchPlane" : qUnion([Q0])});
            skLineSegment(sketch, "E160.bottom", {"start": v(-79.14, 97) * mm, "end": v(-73.44, 97) * mm});
            skLineSegment(sketch, "E160.top", {"start": v(-79.14, 91) * mm, "end": v(-73.44, 91) * mm});
            skLineSegment(sketch, "E160.left", {"start": v(-79.14, 97) * mm, "end": v(-79.14, 91) * mm});
            skLineSegment(sketch, "E160.right", {"start": v(-73.44, 97) * mm, "end": v(-73.44, 91) * mm});
            skLineSegment(sketch, "E161", {"start": v(-118.85, 68.5) * mm, "end": v(29.54, 68.5) * mm, "construction": true});
            skLineSegment(sketch, "E162.MirrorCS", {"start": v(-73.44, 40) * mm, "end": v(-73.44, 46) * mm});
            skLineSegment(sketch, "E163.MirrorCS", {"start": v(-79.14, 40) * mm, "end": v(-79.14, 46) * mm});
            skLineSegment(sketch, "E164.MirrorCS", {"start": v(-79.14, 46) * mm, "end": v(-73.44, 46) * mm});
            skLineSegment(sketch, "E165.MirrorCS", {"start": v(-79.14, 40) * mm, "end": v(-73.44, 40) * mm});
            skSolve(sketch);
        }
        {
            var Q0;
            Q0=qSketchRegion(id+"F28",true);
            extrude(context, id + "F29", {"entities" : qUnion([Q0]), "operationType" : NewBodyOperationType.REMOVE, "endBound" : BoundingType.THROUGH_ALL, "oppositeDirection" : true, "depth" : 25 * mm, "offsetDistance" : 25 * mm});
        }
        {
            var Q0;
            Q0=makeQuery(id+"F29.boolean.opBoolean","COPY",FACE,{"derivedFrom":makeQuery(id+"F29.opExtrude","SWEPT_FACE",FACE,{"disambiguationData":[OSD([sQuery(id+"F28.wireOp",EDGE,"E160.top")])]})});
            var sketch = newSketch(context, id + "F30", { "sketchPlane" : qUnion([Q0])});
            skLineSegment(sketch, "E166", {"start": v(79.14, 2) * mm, "end": v(77.99, 0) * mm});
            skLineSegment(sketch, "E167", {"start": v(77.99, 0) * mm, "end": v(79.14, 0) * mm});
            skLineSegment(sketch, "E168", {"start": v(79.14, 0) * mm, "end": v(79.14, 2) * mm});
            skSolve(sketch);
        }
        {
            var Q0;
            Q0=qSketchRegion(id+"F30",true);
            extrude(context, id + "F31", {"entities" : qUnion([Q0]), "operationType" : NewBodyOperationType.ADD, "depth" : 6 * mm, "offsetDistance" : 25 * mm});
        }
        {
            var Q0;
            Q0=makeQuery(id+"F29.boolean.opBoolean","COPY",FACE,{"derivedFrom":makeQuery(id+"F29.opExtrude","SWEPT_FACE",FACE,{"disambiguationData":[OSD([sQuery(id+"F28.wireOp",EDGE,"E165.MirrorCS")])]})});
            var sketch = newSketch(context, id + "F32", { "sketchPlane" : qUnion([Q0])});
            skLineSegment(sketch, "E169", {"start": v(79.14, 0) * mm, "end": v(79.14, 2) * mm});
            skLineSegment(sketch, "E170", {"start": v(79.14, 2) * mm, "end": v(77.99, 0) * mm});
            skLineSegment(sketch, "E171", {"start": v(77.99, 0) * mm, "end": v(79.14, 0) * mm});
            skSolve(sketch);
        }
        {
            var Q0;
            Q0=qSketchRegion(id+"F32",true);
            extrude(context, id + "F33", {"entities" : qUnion([Q0]), "operationType" : NewBodyOperationType.ADD, "depth" : 6 * mm, "offsetDistance" : 25 * mm});
        }
        {
            var Q0;
            {var subQ6=sQuery(id+"F1.wireOp",EDGE,"E74.right");var subQ8=sQuery(id+"F1.wireOp",EDGE,"E74.top");var subQ11=sQuery(id+"F1.wireOp",EDGE,"E74.left");var subQ14=sQuery(id+"F1.wireOp",EDGE,"E74.bottom");var subQ15=makeQuery(id+"F2.opExtrude","SWEPT_FACE",FACE,{"disambiguationData":[OSD([subQ14])]});Q0=makeQuery(id+"F11.boolean.opBoolean","SPLIT",FACE,{"disambiguationData":[TD([subQ15])],"derivedFrom":makeQuery(id+"F4.boolean.opBoolean","SPLIT",FACE,{"disambiguationData":[TD([subQ15])],"derivedFrom":makeQuery(id+"F2.opExtrude","CAP_FACE",FACE,{"disambiguationData":[OSD([subQ14,subQ8,subQ11,subQ6])],"isStart":false})})});}
            var sketch = newSketch(context, id + "F34", { "sketchPlane" : qUnion([Q0])});
            skCircle(sketch, "E172", {"center": v(-24.7, 127.42) * mm, "radius": 5.25 * mm});
            skSolve(sketch);
        }
        {
            var Q0;
            {var subQ0=sQuery(id+"F1.wireOp",EDGE,"E74.right");var subQ1=sQuery(id+"F1.wireOp",EDGE,"E74.top");var subQ2=sQuery(id+"F1.wireOp",EDGE,"E74.bottom");var subQ3=sQuery(id+"F1.wireOp",EDGE,"E74.left");Q0=makeQuery(id+"FfK5JAkn5u3NgFW_1.boolean.opBoolean","MERGE",FACE,{"derivedFrom":[makeQuery(id+"F5xRZj30ngV5mFo_1.boolean.opBoolean","MERGE",FACE,{"derivedFrom":[makeQuery(id+"F33.boolean.opBoolean","MERGE",FACE,{"derivedFrom":[makeQuery(id+"F31.boolean.opBoolean","MERGE",FACE,{"derivedFrom":[makeQuery(id+"F25.boolean.opBoolean","SPLIT",FACE,{"disambiguationData":[TD([makeQuery(id+"F2.opExtrude","SWEPT_FACE",FACE,{"disambiguationData":[OSD([subQ2])]})])],"derivedFrom":makeQuery(id+"F2.opExtrude","CAP_FACE",FACE,{"disambiguationData":[OSD([subQ2,subQ1,subQ3,subQ0])],"isStart":true})}),makeQuery(id+"F31.opExtrude","SWEPT_FACE",FACE,{"disambiguationData":[OSD([sQuery(id+"F30.wireOp",EDGE,"Ij8CTVFE-o8PY-hqAJ-aZYK-jF80TkOWeCCv")])]})]}),makeQuery(id+"F33.opExtrude","SWEPT_FACE",FACE,{"disambiguationData":[OSD([sQuery(id+"F32.wireOp",EDGE,"Wp6v5WQb-CLe0-0hJ1-DRIM-dP1oPp1I0sgc")])]})]}),makeQuery(id+"F5xRZj30ngV5mFo_1.opExtrude","SWEPT_FACE",FACE,{"disambiguationData":[OSD([sQuery(id+"FohgaEfprzxjLsH_1.wireOp",EDGE,"khYEeyqB-kWyY-8gIr-LFha-HESkmTz9Muqk")])]})]}),makeQuery(id+"FfK5JAkn5u3NgFW_1.opExtrude","SWEPT_FACE",FACE,{"disambiguationData":[OSD([sQuery(id+"FQOiN2EmPNX4Zff_1.wireOp",EDGE,"xRaGVgji-VYYc-Lk9T-zl6b-8iJrfARz3ZKq")])]})]});}
            var sketch = newSketch(context, id + "F35", { "sketchPlane" : qUnion([Q0])});
            skCircle(sketch, "E173", {"center": v(-24.7, -127.42) * mm, "radius": 6.5 * mm});
            skSolve(sketch);
        }
        {
            var Q1;
            Q1=qSketchRegion(id+"F34",true);
            var Q2;
            Q2=qSketchRegion(id+"F35",true);
            loft(context, id + "F36", {"operationType" : NewBodyOperationType.REMOVE, "sheetProfilesArray" : [{ "sheetProfileEntities" : qUnion([Q1]) }, { "sheetProfileEntities" : qUnion([Q2]) }]});
        }
        {
            var Q0;
            {var subQ6=sQuery(id+"F1.wireOp",EDGE,"E74.right");var subQ8=sQuery(id+"F1.wireOp",EDGE,"E74.top");var subQ11=sQuery(id+"F1.wireOp",EDGE,"E74.left");var subQ14=sQuery(id+"F1.wireOp",EDGE,"E74.bottom");var subQ15=makeQuery(id+"F2.opExtrude","SWEPT_FACE",FACE,{"disambiguationData":[OSD([subQ14])]});Q0=makeQuery(id+"F11.boolean.opBoolean","SPLIT",FACE,{"disambiguationData":[TD([subQ15])],"derivedFrom":makeQuery(id+"F4.boolean.opBoolean","SPLIT",FACE,{"disambiguationData":[TD([subQ15])],"derivedFrom":makeQuery(id+"F2.opExtrude","CAP_FACE",FACE,{"disambiguationData":[OSD([subQ14,subQ8,subQ11,subQ6])],"isStart":false})})});}
            var sketch = newSketch(context, id + "F37", { "sketchPlane" : qUnion([Q0])});
            skCircle(sketch, "E174", {"center": v(-24.7, 9.58) * mm, "radius": 5.25 * mm});
            skSolve(sketch);
        }
        {
            var Q0;
            {var subQ0=sQuery(id+"F1.wireOp",EDGE,"E74.right");var subQ1=sQuery(id+"F1.wireOp",EDGE,"E74.top");var subQ2=sQuery(id+"F1.wireOp",EDGE,"E74.bottom");var subQ3=sQuery(id+"F1.wireOp",EDGE,"E74.left");Q0=makeQuery(id+"FfK5JAkn5u3NgFW_1.boolean.opBoolean","MERGE",FACE,{"derivedFrom":[makeQuery(id+"F5xRZj30ngV5mFo_1.boolean.opBoolean","MERGE",FACE,{"derivedFrom":[makeQuery(id+"F33.boolean.opBoolean","MERGE",FACE,{"derivedFrom":[makeQuery(id+"F31.boolean.opBoolean","MERGE",FACE,{"derivedFrom":[makeQuery(id+"F25.boolean.opBoolean","SPLIT",FACE,{"disambiguationData":[TD([makeQuery(id+"F2.opExtrude","SWEPT_FACE",FACE,{"disambiguationData":[OSD([subQ2])]})])],"derivedFrom":makeQuery(id+"F2.opExtrude","CAP_FACE",FACE,{"disambiguationData":[OSD([subQ2,subQ1,subQ3,subQ0])],"isStart":true})}),makeQuery(id+"F31.opExtrude","SWEPT_FACE",FACE,{"disambiguationData":[OSD([sQuery(id+"F30.wireOp",EDGE,"Ij8CTVFE-o8PY-hqAJ-aZYK-jF80TkOWeCCv")])]})]}),makeQuery(id+"F33.opExtrude","SWEPT_FACE",FACE,{"disambiguationData":[OSD([sQuery(id+"F32.wireOp",EDGE,"Wp6v5WQb-CLe0-0hJ1-DRIM-dP1oPp1I0sgc")])]})]}),makeQuery(id+"F5xRZj30ngV5mFo_1.opExtrude","SWEPT_FACE",FACE,{"disambiguationData":[OSD([sQuery(id+"FohgaEfprzxjLsH_1.wireOp",EDGE,"khYEeyqB-kWyY-8gIr-LFha-HESkmTz9Muqk")])]})]}),makeQuery(id+"FfK5JAkn5u3NgFW_1.opExtrude","SWEPT_FACE",FACE,{"disambiguationData":[OSD([sQuery(id+"FQOiN2EmPNX4Zff_1.wireOp",EDGE,"xRaGVgji-VYYc-Lk9T-zl6b-8iJrfARz3ZKq")])]})]});}
            var sketch = newSketch(context, id + "F38", { "sketchPlane" : qUnion([Q0])});
            skCircle(sketch, "E175", {"center": v(-24.7, -9.58) * mm, "radius": 6.5 * mm});
            skSolve(sketch);
        }
        {
            var Q1;
            Q1=qSketchRegion(id+"F37",true);
            var Q2;
            Q2=qSketchRegion(id+"F38",true);
            loft(context, id + "F39", {"operationType" : NewBodyOperationType.REMOVE, "sheetProfilesArray" : [{ "sheetProfileEntities" : qUnion([Q1]) }, { "sheetProfileEntities" : qUnion([Q2]) }]});
        }
        {
            var Q0;
            {var subQ1=sQuery(id+"F3.wireOp",EDGE,"E78.bottom");Q0=makeQuery(id+"F4.boolean.opBoolean","SPLIT",FACE,{"disambiguationData":[TD([makeQuery(id+"F4.opExtrude","SWEPT_FACE",FACE,{"disambiguationData":[OSD([subQ1])]})])],"derivedFrom":makeQuery(id+"F2.opExtrude","CAP_FACE",FACE,{"disambiguationData":[OSD([sQuery(id+"F1.wireOp",EDGE,"E74.bottom"),sQuery(id+"F1.wireOp",EDGE,"E74.top"),sQuery(id+"F1.wireOp",EDGE,"E74.left"),sQuery(id+"F1.wireOp",EDGE,"E74.right")])],"isStart":false})});}
            var sketch = newSketch(context, id + "F40", { "sketchPlane" : qUnion([Q0])});
            skLineSegment(sketch, "E176", {"start": v(-61.7, 97.44) * mm, "end": v(-62.7, 97.44) * mm});
            skLineSegment(sketch, "E177", {"start": v(-62.7, 90.44) * mm, "end": v(-61.7, 90.44) * mm});
            skLineSegment(sketch, "E178", {"start": v(-61.7, 90.44) * mm, "end": v(-61.7, 91.44) * mm});
            skLineSegment(sketch, "E179", {"start": v(-61.7, 91.44) * mm, "end": v(-62.7, 91.44) * mm});
            skLineSegment(sketch, "E180", {"start": v(-62.7, 96.44) * mm, "end": v(-61.7, 96.44) * mm});
            skLineSegment(sketch, "E181", {"start": v(-61.7, 96.44) * mm, "end": v(-61.7, 97.44) * mm});
            skLineSegment(sketch, "E182", {"start": v(-62.7, 45.56) * mm, "end": v(-61.7, 45.56) * mm});
            skLineSegment(sketch, "E183", {"start": v(-61.7, 45.56) * mm, "end": v(-61.7, 46.56) * mm});
            skLineSegment(sketch, "E184", {"start": v(-61.7, 46.56) * mm, "end": v(-62.7, 46.56) * mm});
            skLineSegment(sketch, "E185", {"start": v(-62.7, 39.56) * mm, "end": v(-61.7, 39.56) * mm});
            skLineSegment(sketch, "E186", {"start": v(-61.7, 39.56) * mm, "end": v(-61.7, 40.56) * mm});
            skLineSegment(sketch, "E187", {"start": v(-61.7, 40.56) * mm, "end": v(-62.7, 40.56) * mm});
            skLineSegment(sketch, "E188", {"start": v(-62.7, 97.44) * mm, "end": v(-62.7, 96.44) * mm});
            skLineSegment(sketch, "E189", {"start": v(-62.7, 91.44) * mm, "end": v(-62.7, 90.44) * mm});
            skLineSegment(sketch, "E190", {"start": v(-62.7, 46.56) * mm, "end": v(-62.7, 45.56) * mm});
            skLineSegment(sketch, "E191", {"start": v(-62.7, 40.56) * mm, "end": v(-62.7, 39.56) * mm});
            skSolve(sketch);
        }
        {
            var Q0;
            Q0=qSketchRegion(id+"F40",true);
            extrude(context, id + "F41", {"entities" : qUnion([Q0]), "operationType" : NewBodyOperationType.ADD, "depth" : 5 * mm, "offsetDistance" : 25 * mm});
        }
        {
            var Q0;
            Q0=makeQuery(id+"F41.boolean.opBoolean","MERGE",FACE,{"derivedFrom":[makeQuery(id+"F4.opExtrude","CAP_FACE",FACE,{"disambiguationData":[OSD([sQuery(id+"F3.wireOp",EDGE,"E75.bottom"),sQuery(id+"F3.wireOp",EDGE,"E75.top"),sQuery(id+"F3.wireOp",EDGE,"E75.left"),sQuery(id+"F3.wireOp",EDGE,"E75.right"),sQuery(id+"F3.wireOp",EDGE,"E78.bottom"),sQuery(id+"F3.wireOp",EDGE,"E78.top"),sQuery(id+"F3.wireOp",EDGE,"E78.left"),sQuery(id+"F3.wireOp",EDGE,"E78.right"),sQuery(id+"F3.wireOp",EDGE,"E80.bottom"),sQuery(id+"F3.wireOp",EDGE,"E80.top"),sQuery(id+"F3.wireOp",EDGE,"E80.left"),sQuery(id+"F3.wireOp",EDGE,"E80.right"),sQuery(id+"F3.wireOp",EDGE,"E83.bottom"),sQuery(id+"F3.wireOp",EDGE,"E83.top"),sQuery(id+"F3.wireOp",EDGE,"E83.left"),sQuery(id+"F3.wireOp",EDGE,"E84"),sQuery(id+"F3.wireOp",EDGE,"E85"),sQuery(id+"F3.wireOp",EDGE,"E86"),sQuery(id+"F3.wireOp",EDGE,"E87"),sQuery(id+"F3.wireOp",EDGE,"E88"),sQuery(id+"F3.wireOp",EDGE,"E89"),sQuery(id+"F3.wireOp",EDGE,"E90"),sQuery(id+"F3.wireOp",EDGE,"E91"),sQuery(id+"F3.wireOp",EDGE,"E92"),sQuery(id+"F3.wireOp",EDGE,"E93")])],"isStart":false}),makeQuery(id+"F41.opExtrude","CAP_FACE",FACE,{"disambiguationData":[OSD([sQuery(id+"F40.wireOp",EDGE,"E176"),sQuery(id+"F40.wireOp",EDGE,"E180"),sQuery(id+"F40.wireOp",EDGE,"E181"),sQuery(id+"F40.wireOp",EDGE,"E188")])],"isStart":false}),makeQuery(id+"F41.opExtrude","CAP_FACE",FACE,{"disambiguationData":[OSD([sQuery(id+"F40.wireOp",EDGE,"E177"),sQuery(id+"F40.wireOp",EDGE,"E178"),sQuery(id+"F40.wireOp",EDGE,"E179"),sQuery(id+"F40.wireOp",EDGE,"E189")])],"isStart":false})]});
            var sketch = newSketch(context, id + "F42", { "sketchPlane" : qUnion([Q0])});
            skLineSegment(sketch, "E192.bottom", {"start": v(-22.8, 102.84) * mm, "end": v(-14, 102.84) * mm});
            skLineSegment(sketch, "E192.top", {"start": v(-22.8, 104.24) * mm, "end": v(-14, 104.24) * mm});
            skLineSegment(sketch, "E192.left", {"start": v(-22.8, 102.84) * mm, "end": v(-22.8, 104.24) * mm});
            skLineSegment(sketch, "E192.right", {"start": v(-14, 102.84) * mm, "end": v(-14, 104.24) * mm});
            skLineSegment(sketch, "E193.bottom", {"start": v(-22.8, 51.96) * mm, "end": v(-14, 51.96) * mm});
            skLineSegment(sketch, "E193.top", {"start": v(-22.8, 53.36) * mm, "end": v(-14, 53.36) * mm});
            skLineSegment(sketch, "E193.left", {"start": v(-22.8, 51.96) * mm, "end": v(-22.8, 53.36) * mm});
            skLineSegment(sketch, "E193.right", {"start": v(-14, 51.96) * mm, "end": v(-14, 53.36) * mm});
            skSolve(sketch);
        }
        {
            var Q0;
            Q0=qSketchRegion(id+"F42",true);
            extrude(context, id + "F43", {"entities" : qUnion([Q0]), "operationType" : NewBodyOperationType.REMOVE, "oppositeDirection" : true, "depth" : 6 * mm, "offsetDistance" : 25 * mm});
        }
        {
            var Q0;
            {var subQ1=sQuery(id+"F3.wireOp",EDGE,"E83.left");Q0=makeQuery(id+"F41.boolean.opBoolean","SPLIT",FACE,{"disambiguationData":[TD([makeQuery(id+"F27.boolean.opBoolean","COPY",FACE,{"derivedFrom":makeQuery(id+"F27.opExtrude","SWEPT_FACE",FACE,{"disambiguationData":[OSD([sQuery(id+"F26.wireOp",EDGE,"E159.bottom")])]})})])],"derivedFrom":makeQuery(id+"F27.boolean.opBoolean","MERGE",FACE,{"derivedFrom":[makeQuery(id+"F4.opExtrude","SWEPT_FACE",FACE,{"disambiguationData":[OSD([subQ1])]}),makeQuery(id+"F27.opExtrude","SWEPT_FACE",FACE,{"disambiguationData":[OSD([sQuery(id+"F26.wireOp",EDGE,"E159.right")])]})]})});}
            var sketch = newSketch(context, id + "F44", { "sketchPlane" : qUnion([Q0])});
            skLineSegment(sketch, "E194.bottom", {"start": v(-91.44, 7) * mm, "end": v(-96.44, 7) * mm});
            skLineSegment(sketch, "E194.top", {"start": v(-91.44, 6) * mm, "end": v(-96.44, 6) * mm});
            skLineSegment(sketch, "E194.left", {"start": v(-91.44, 7) * mm, "end": v(-91.44, 6) * mm});
            skLineSegment(sketch, "E194.right", {"start": v(-96.44, 7) * mm, "end": v(-96.44, 6) * mm});
            skLineSegment(sketch, "E195.bottom", {"start": v(-45.56, 7) * mm, "end": v(-40.56, 7) * mm});
            skLineSegment(sketch, "E195.top", {"start": v(-45.56, 6) * mm, "end": v(-40.56, 6) * mm});
            skLineSegment(sketch, "E195.left", {"start": v(-45.56, 7) * mm, "end": v(-45.56, 6) * mm});
            skLineSegment(sketch, "E195.right", {"start": v(-40.56, 7) * mm, "end": v(-40.56, 6) * mm});
            skSolve(sketch);
        }
        {
            var Q0;
            Q0=qSketchRegion(id+"F44",true);
            extrude(context, id + "F45", {"entities" : qUnion([Q0]), "operationType" : NewBodyOperationType.ADD, "depth" : 1 * mm, "offsetDistance" : 25 * mm});
        }
        {
            var Q0;
            Q0=makeQuery(id+"F45.boolean.opBoolean","MERGE",FACE,{"derivedFrom":[makeQuery(id+"F41.boolean.opBoolean","MERGE",FACE,{"derivedFrom":[makeQuery(id+"F4.opExtrude","CAP_FACE",FACE,{"disambiguationData":[OSD([sQuery(id+"F3.wireOp",EDGE,"E75.bottom"),sQuery(id+"F3.wireOp",EDGE,"E75.top"),sQuery(id+"F3.wireOp",EDGE,"E75.left"),sQuery(id+"F3.wireOp",EDGE,"E75.right"),sQuery(id+"F3.wireOp",EDGE,"E78.bottom"),sQuery(id+"F3.wireOp",EDGE,"E78.top"),sQuery(id+"F3.wireOp",EDGE,"E78.left"),sQuery(id+"F3.wireOp",EDGE,"E78.right"),sQuery(id+"F3.wireOp",EDGE,"E80.bottom"),sQuery(id+"F3.wireOp",EDGE,"E80.top"),sQuery(id+"F3.wireOp",EDGE,"E80.left"),sQuery(id+"F3.wireOp",EDGE,"E80.right"),sQuery(id+"F3.wireOp",EDGE,"E83.bottom"),sQuery(id+"F3.wireOp",EDGE,"E83.top"),sQuery(id+"F3.wireOp",EDGE,"E83.left"),sQuery(id+"F3.wireOp",EDGE,"E84"),sQuery(id+"F3.wireOp",EDGE,"E85"),sQuery(id+"F3.wireOp",EDGE,"E86"),sQuery(id+"F3.wireOp",EDGE,"E87"),sQuery(id+"F3.wireOp",EDGE,"E88"),sQuery(id+"F3.wireOp",EDGE,"E89"),sQuery(id+"F3.wireOp",EDGE,"E90"),sQuery(id+"F3.wireOp",EDGE,"E91"),sQuery(id+"F3.wireOp",EDGE,"E92"),sQuery(id+"F3.wireOp",EDGE,"E93")])],"isStart":false}),makeQuery(id+"F41.opExtrude","CAP_FACE",FACE,{"disambiguationData":[OSD([sQuery(id+"F40.wireOp",EDGE,"E176"),sQuery(id+"F40.wireOp",EDGE,"E180"),sQuery(id+"F40.wireOp",EDGE,"E181"),sQuery(id+"F40.wireOp",EDGE,"E188")])],"isStart":false}),makeQuery(id+"F41.opExtrude","CAP_FACE",FACE,{"disambiguationData":[OSD([sQuery(id+"F40.wireOp",EDGE,"E177"),sQuery(id+"F40.wireOp",EDGE,"E178"),sQuery(id+"F40.wireOp",EDGE,"E179"),sQuery(id+"F40.wireOp",EDGE,"E189")])],"isStart":false})]}),makeQuery(id+"F45.opExtrude","SWEPT_FACE",FACE,{"disambiguationData":[OSD([sQuery(id+"F44.wireOp",EDGE,"E194.bottom")])]})]});
            var sketch = newSketch(context, id + "F46", { "sketchPlane" : qUnion([Q0])});
            skLineSegment(sketch, "E196", {"start": v(-5, 115.5) * mm, "end": v(0, 112.61) * mm});
            skLineSegment(sketch, "E197", {"start": v(0, 112.61) * mm, "end": v(0, 115.5) * mm});
            skLineSegment(sketch, "E198", {"start": v(0, 115.5) * mm, "end": v(-5, 115.5) * mm});
            skLineSegment(sketch, "E199", {"start": v(0, 75.39) * mm, "end": v(-5, 72.5) * mm});
            skLineSegment(sketch, "E200", {"start": v(-5, 72.5) * mm, "end": v(0, 72.5) * mm});
            skLineSegment(sketch, "E201", {"start": v(0, 72.5) * mm, "end": v(0, 75.39) * mm});
            skLineSegment(sketch, "E202", {"start": v(-5, 64.5) * mm, "end": v(0, 61.61) * mm});
            skLineSegment(sketch, "E203", {"start": v(0, 61.61) * mm, "end": v(0, 64.5) * mm});
            skLineSegment(sketch, "E204", {"start": v(0, 64.5) * mm, "end": v(-5, 64.5) * mm});
            skLineSegment(sketch, "E205", {"start": v(0, 24.39) * mm, "end": v(-5, 21.5) * mm});
            skLineSegment(sketch, "E206", {"start": v(-5, 21.5) * mm, "end": v(0, 21.5) * mm});
            skLineSegment(sketch, "E207", {"start": v(0, 21.5) * mm, "end": v(0, 24.39) * mm});
            skSolve(sketch);
        }
        {
            var Q0;
            Q0=qSketchRegion(id+"F46",true);
            extrude(context, id + "F47", {"entities" : qUnion([Q0]), "operationType" : NewBodyOperationType.REMOVE, "oppositeDirection" : true, "depth" : 5 * mm, "offsetDistance" : 25 * mm});
        }
    });
